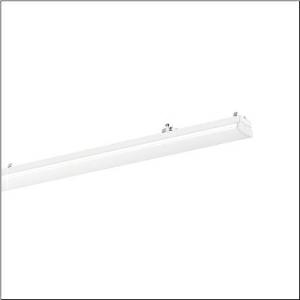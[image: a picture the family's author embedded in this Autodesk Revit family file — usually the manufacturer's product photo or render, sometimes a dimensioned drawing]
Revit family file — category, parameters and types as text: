
# Revit family: licross_r__11_recessed_opal_mo_51tl1dcn485g_363e
name_source: partatom
category: Lighting Fixtures
units: mm (PartAtom-declared; Revit-internal decimal feet)

## family parameters
Cut with Voids When Loaded = No
Host = Face
Light Source = No
Part Type = Normal
Room Calculation Point = No
Round Connector Dimension = Use Diameter
Shared = No

## types (1)
- --- (1 x LED, 8820 lm, 49.3 W, 4000K)
    Apparent Load = 49 VA
    CIE Flux Codes = 44 73 91 87 100
    Color Rendering = 80
    Color Temperature = 4000K
    Default Elevation = 1800 mm
    Description = Licross® 11 recessed opal MO, luminaire insert, of sheet steel, coil coated, white, length: 1.500mm, width: 76mm, height: 87mm, LED rated luminous flux: 8.820lm, light colour: 840, control gear: ON/OFF Multilumen, CLOi, with plug, 3-pole, with phase selection, mains connection: 220..240V, AC, 50/60Hz, start of lifetime: 49W, end of service life: 55W, internal wiring halogen-free, primary optical cover: cover, of PMMA, light emission: direct with ceiling illumination distribution, primary light characteristic: symmetric, protection rating (complete): IP40, insulation class (complete): insulation class I (protective earthing), certification: CE, ENEC, VDE, UKCA, protection symbol: D if used in an environment without relevant dust loads with corresponding accessories, impact resistance: IK06, permissible ambient temperature for indoor applications: -35..+40°C, corresponds to IFS (International Featured Standards) requirements for safety and quality in the food industry, reducing of maximum allowable ambient temperature of 5°C with ceiling mounting, LABS conformity tested according to VDMA 24364:2018-05, packaging unit: 1 piece
    Height = 83 mm
    Lamp = 1 x LED
    Lamp Light Flux = 8820 lm
    Lamp Power = 49.3 W
    Lamp count = 1
    Length = 1500 mm
    Luminous efficacy = 179 lm/W
    Manufacturer = Siteco
    ModVariant = No
    Model = 51TL1DCN485G
    Mounting Place = Ceiling
    Mounting Type = Pendant
    Number of Poles = 1
    OnlyDefault = Yes
    Power Factor = 1
    Product Name = Licross® 11 recessed opal MO
    Product group = luminaire insert | ceiling pendant
    ProductGroupID = 902
    Protection Class = Protection class I
    Protection Degree = IP 40
    RLX_Detail_Level = 1
    RLX_Emergency_Light_Flux = 0 lm
    RLX_Emergency_Type = 0
    RLX_Emergency_Type_DB = No
    RlxData = <blob elided: 24613 chars, md5=be2697ae>
    Socket = socket
    Standby Power = 0 W
    System Light Flux = 8820 lm
    System Power = 49 W
    Type Comments = factory setting: luminous flux: 100 % | (A | C | E) | 113 mA
    Type Image = l_1313666.jpg
    URL = http://relux.com
    VarID = @adj_089893
    Voltage = 0 V
    Weight = 0.00 kg
    Width = 76 mm

## geometry (parser evidence)
native form markers: Blend x4, Sweep x13
no freeform markers — native parametric forms only
